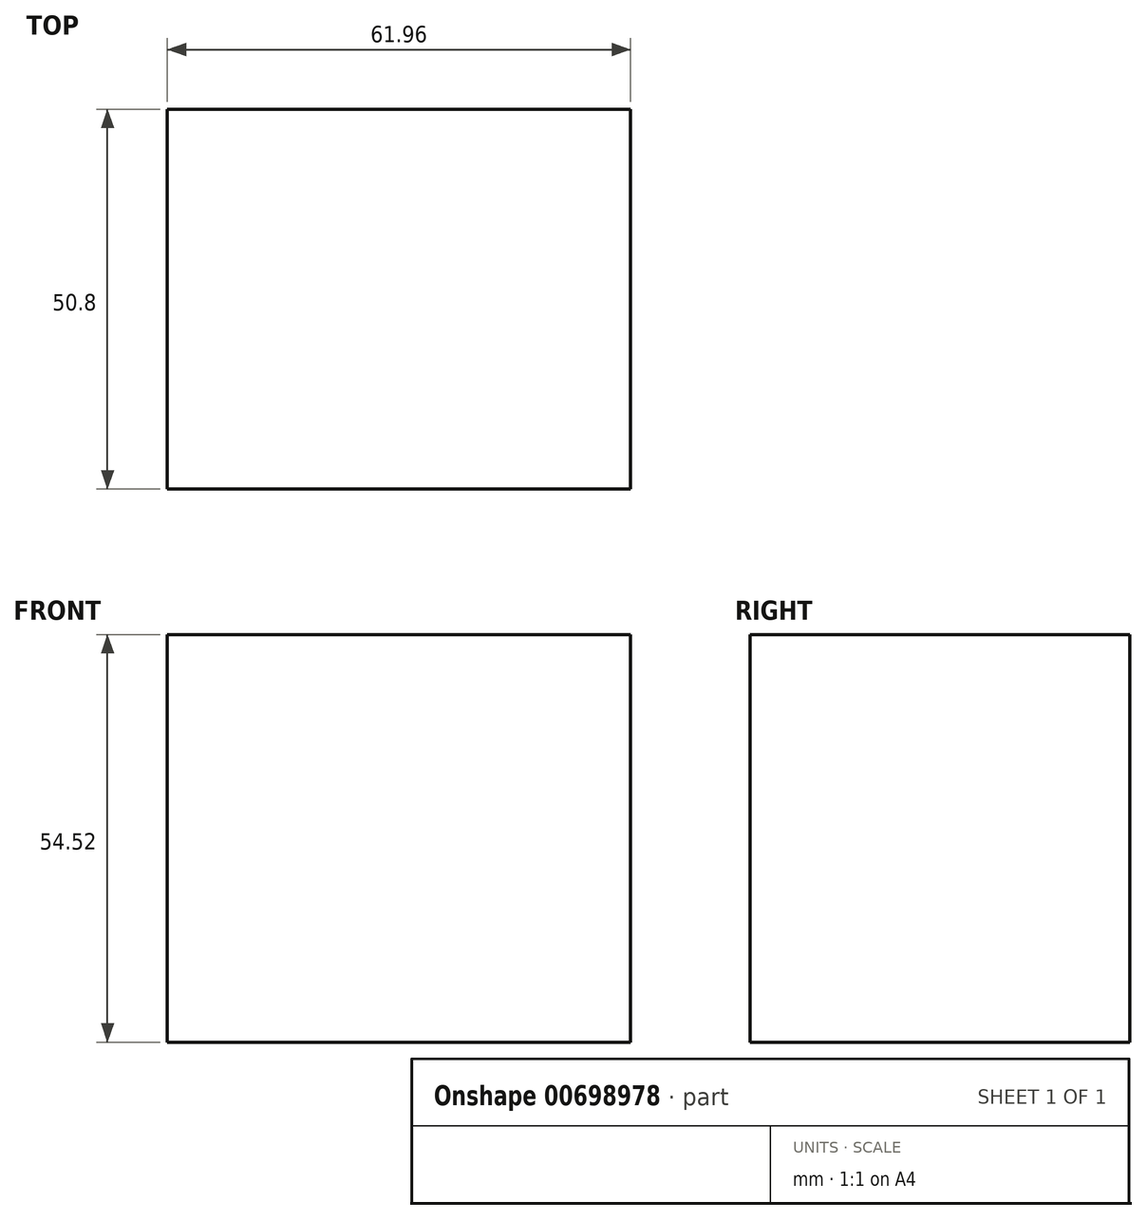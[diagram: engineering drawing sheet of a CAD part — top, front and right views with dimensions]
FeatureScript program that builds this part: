
annotation { "Feature Type Name" : "Feature", "Feature Type Description" : "" }
export const myFeature = defineFeature(function(context is Context, id is Id, definition is map)
    precondition{}
    {
        {
            var Q0;
            Q0=qCreatedBy(makeId("Front.planeOp"),FACE);
            var sketch = newSketch(context, id + "F0", { "sketchPlane" : qUnion([Q0])});
            skLineSegment(sketch, "E0.bottom", {"start": v(-30.98, 27.26) * mm, "end": v(30.98, 27.26) * mm});
            skLineSegment(sketch, "E0.top", {"start": v(-30.98, -27.26) * mm, "end": v(30.98, -27.26) * mm});
            skLineSegment(sketch, "E0.left", {"start": v(-30.98, 27.26) * mm, "end": v(-30.98, -27.26) * mm});
            skLineSegment(sketch, "E0.right", {"start": v(30.98, 27.26) * mm, "end": v(30.98, -27.26) * mm});
            skPoint(sketch, "E0.middle", {"position": v(0, 0) * mm});
            skSolve(sketch);
        }
        {
            var Q0;
            Q0=makeQuery(id+"F0.imprint","IMPRINT",FACE,{"disambiguationData":[TD([[makeQuery(id+"F0.imprint","IMPRINT",EDGE,{"derivedFrom":sQuery(id+"F0.wireOp",EDGE,"E0.bottom")}),-1.0]])]});
            extrude(context, id + "F1", {"entities" : qUnion([Q0]), "endBound" : BoundingType.SYMMETRIC, "depth" : 50.8 * mm, "offsetDistance" : 25.4 * mm});
        }
    });
